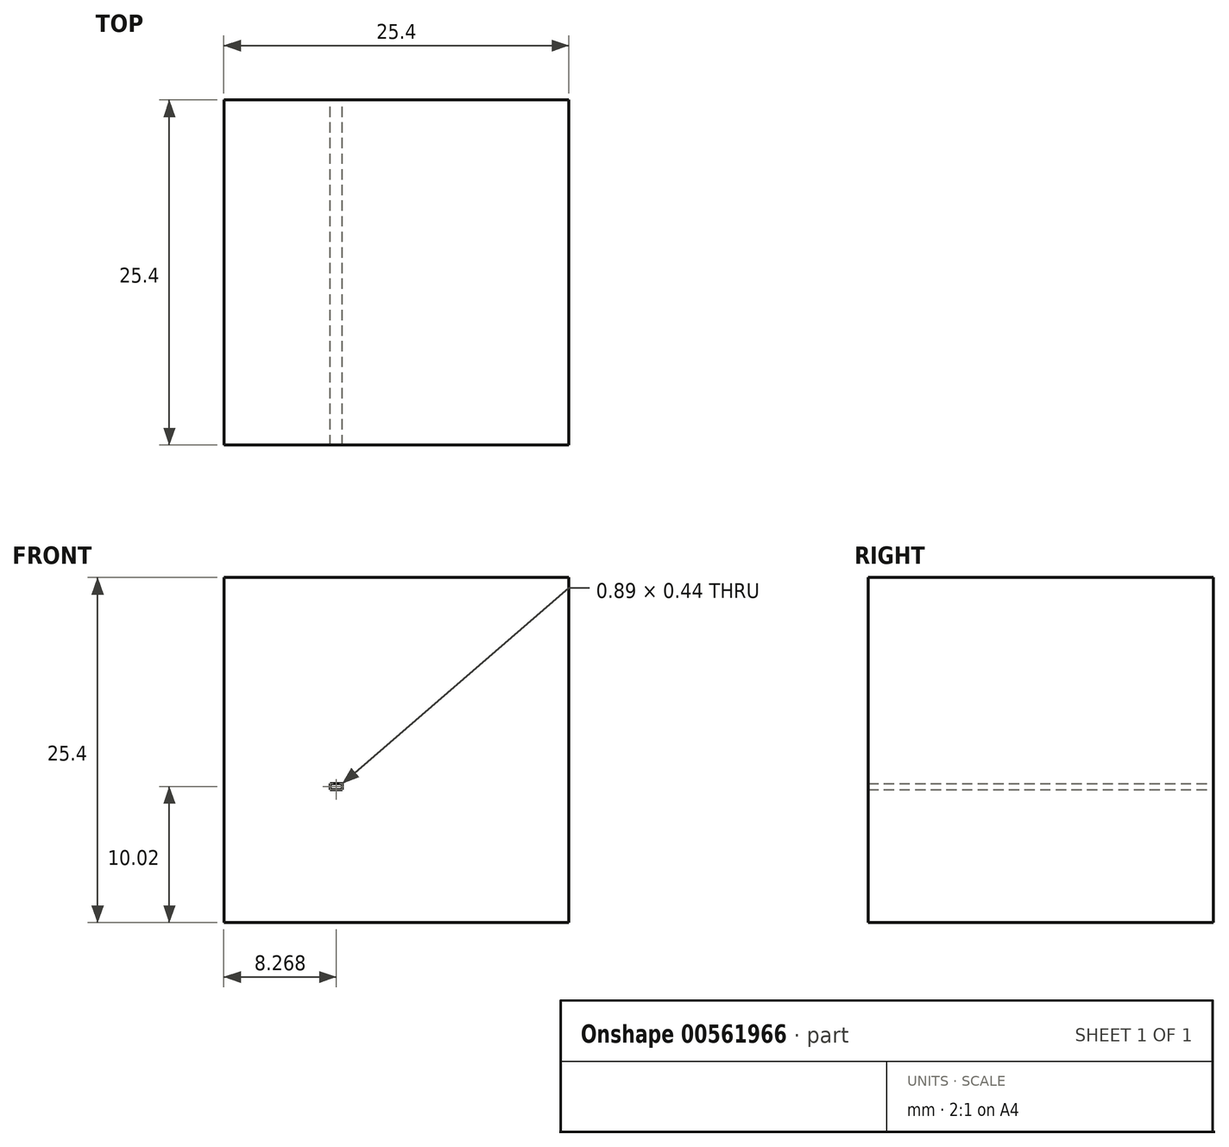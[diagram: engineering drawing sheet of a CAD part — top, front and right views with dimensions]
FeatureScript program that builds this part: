
annotation { "Feature Type Name" : "Feature", "Feature Type Description" : "" }
export const myFeature = defineFeature(function(context is Context, id is Id, definition is map)
    precondition{}
    {
        {
            var Q0;
            Q0=qCreatedBy(makeId("Front.planeOp"),FACE);
            var sketch = newSketch(context, id + "F0", { "sketchPlane" : qUnion([Q0])});
            skLineSegment(sketch, "E0.bottom", {"start": v(-27.38, 43.71) * mm, "end": v(-1.98, 43.71) * mm});
            skLineSegment(sketch, "E0.top", {"start": v(-27.38, 18.31) * mm, "end": v(-1.98, 18.31) * mm});
            skLineSegment(sketch, "E0.left", {"start": v(-27.38, 43.71) * mm, "end": v(-27.38, 18.31) * mm});
            skLineSegment(sketch, "E0.right", {"start": v(-1.98, 43.71) * mm, "end": v(-1.98, 18.31) * mm});
            skLineSegment(sketch, "E1.bottom", {"start": v(-18.67, 28.55) * mm, "end": v(-19.56, 28.55) * mm});
            skLineSegment(sketch, "E1.top", {"start": v(-18.67, 28.1) * mm, "end": v(-19.56, 28.1) * mm});
            skLineSegment(sketch, "E1.left", {"start": v(-18.67, 28.55) * mm, "end": v(-18.67, 28.1) * mm});
            skLineSegment(sketch, "E1.right", {"start": v(-19.56, 28.55) * mm, "end": v(-19.56, 28.1) * mm});
            skSolve(sketch);
        }
        {
            var Q0;
            Q0=makeQuery(id+"F0.imprint","IMPRINT",FACE,{"disambiguationData":[TD([[makeQuery(id+"F0.imprint","IMPRINT",EDGE,{"derivedFrom":sQuery(id+"F0.wireOp",EDGE,"E0.bottom")}),-1.0]])]});
            extrude(context, id + "F1", {"entities" : qUnion([Q0]), "depth" : 25.4 * mm, "offsetDistance" : 25.4 * mm});
        }
    });
